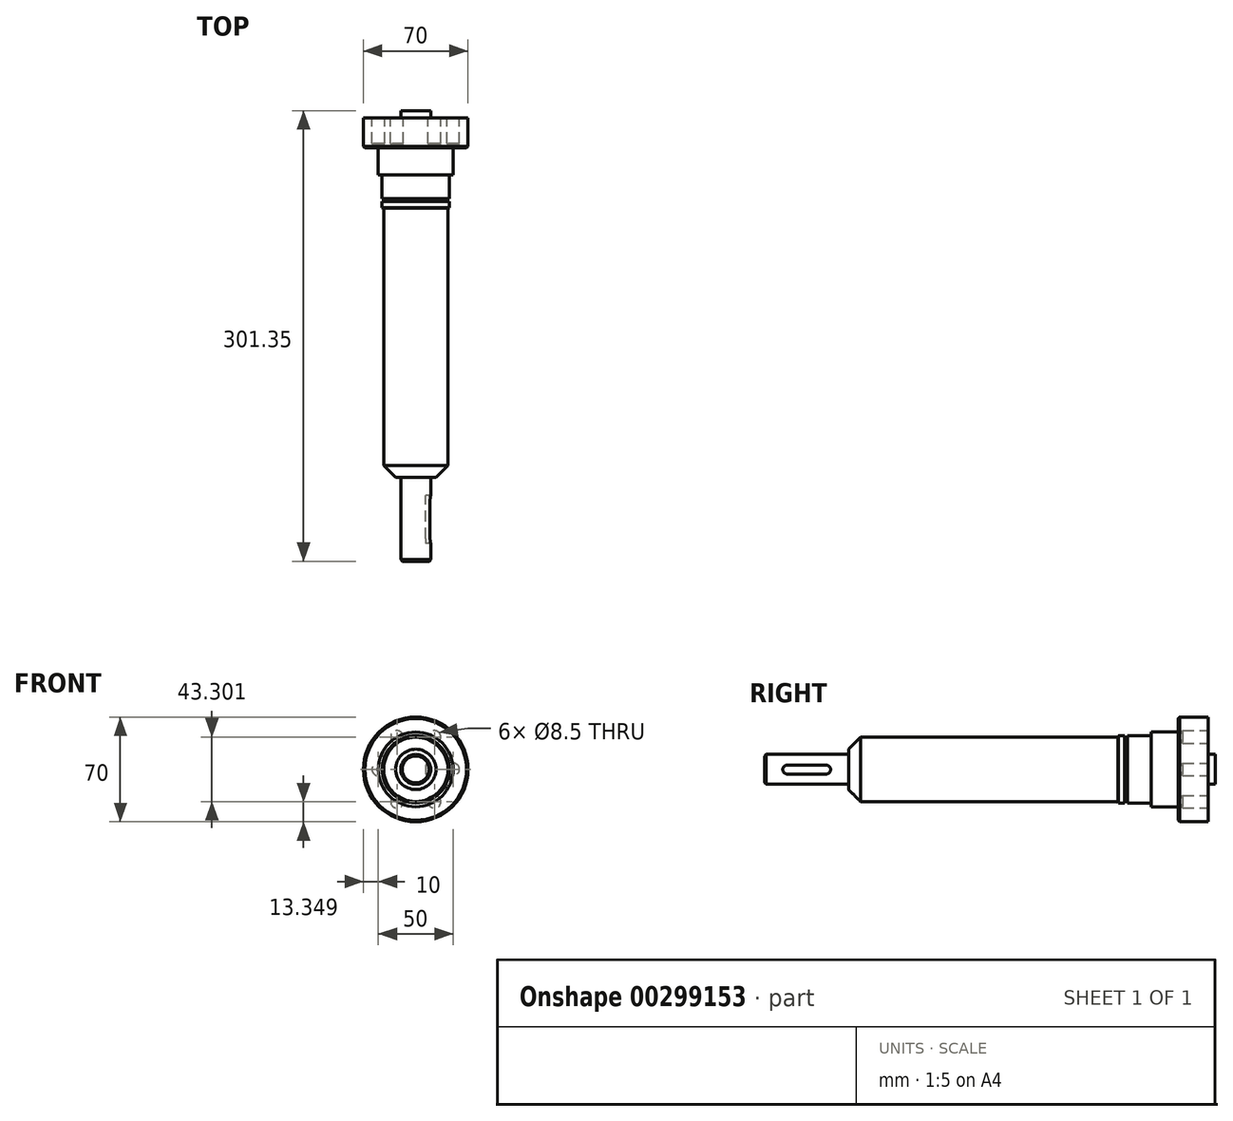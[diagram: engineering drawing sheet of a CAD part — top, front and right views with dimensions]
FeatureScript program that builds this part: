
annotation { "Feature Type Name" : "Feature", "Feature Type Description" : "" }
export const myFeature = defineFeature(function(context is Context, id is Id, definition is map)
    precondition{}
    {
        {
            var Q0;
            Q0=qCreatedBy(makeId("Front.planeOp"),FACE);
            var sketch = newSketch(context, id + "F0", { "sketchPlane" : qUnion([Q0])});
            skCircle(sketch, "E0", {"center": v(0, 0) * mm, "radius": 10 * mm});
            skSolve(sketch);
        }
        {
            var Q0;
            Q0 = qSketchRegion(id + "F0", true);
            extrude(context, id + "F1", {"entities" : qUnion([Q0]), "depth" : 56 * mm});
        }
        {
            var Q0;
            Q0=qCreatedBy(makeId("Front.planeOp"),FACE);
            var sketch = newSketch(context, id + "F2", { "sketchPlane" : qUnion([Q0])});
            skCircle(sketch, "E1", {"center": v(0, 0) * mm, "radius": 21.5 * mm});
            skSolve(sketch);
        }
        {
            var Q0;
            Q0 = qSketchRegion(id + "F2", true);
            extrude(context, id + "F3", {"entities" : qUnion([Q0]), "operationType" : NewBodyOperationType.ADD, "oppositeDirection" : true, "depth" : 180 * mm});
        }
        {
            var Q0;
            Q0=makeQuery(id+"F3.opExtrude","CAP_EDGE",EDGE,{"disambiguationData":[OSD([sQuery(id+"F2.wireOp",EDGE,"E1")])],"isStart":true});
            chamfer(context, id + "F4", {"entities" : qUnion([Q0]), "width" : 8 * mm, "tangentPropagation" : true});
        }
        {
            var Q0;
            Q0=makeQuery(id+"F3.opExtrude","CAP_FACE",FACE,{"disambiguationData":[OSD([sQuery(id+"F2.wireOp",EDGE,"E1")])],"isStart":false});
            cPlane(context, id + "F5", {"entities" : qUnion([Q0]), "cplaneType" : CPlaneType.OFFSET, "offset" : 0 * mm, "width" : 150 * mm, "height" : 150 * mm});
        }
        {
            var Q0;
            Q0=qCreatedBy(id+"F5.planeOp",FACE);
            var sketch = newSketch(context, id + "F6", { "sketchPlane" : qUnion([Q0])});
            skCircle(sketch, "E2", {"center": v(0, 0) * mm, "radius": 22.5 * mm});
            skSolve(sketch);
        }
        {
            var Q0;
            Q0 = qSketchRegion(id + "F6", true);
            extrude(context, id + "F7", {"entities" : qUnion([Q0]), "operationType" : NewBodyOperationType.ADD, "depth" : 40.35 * mm});
        }
        {
            var Q0;
            Q0=makeQuery(id+"F7.opExtrude","CAP_FACE",FACE,{"disambiguationData":[OSD([sQuery(id+"F6.wireOp",EDGE,"E2")])],"isStart":false});
            var sketch = newSketch(context, id + "F8", { "sketchPlane" : qUnion([Q0])});
            skCircle(sketch, "E3", {"center": v(0, 0) * mm, "radius": 35 * mm});
            skSolve(sketch);
        }
        {
            var Q0;
            Q0 = qSketchRegion(id + "F8", true);
            extrude(context, id + "F9", {"entities" : qUnion([Q0]), "operationType" : NewBodyOperationType.ADD, "depth" : 20 * mm});
        }
        {
            var Q0;
            Q0=qCreatedBy(id+"F5.planeOp",FACE);
            cPlane(context, id + "F10", {"entities" : qUnion([Q0]), "cplaneType" : CPlaneType.OFFSET, "offset" : 4.5 * mm, "width" : 150 * mm, "height" : 150 * mm});
        }
        {
            var Q0;
            Q0=qCreatedBy(id+"F10.planeOp",FACE);
            var sketch = newSketch(context, id + "F11", { "sketchPlane" : qUnion([Q0])});
            skCircle(sketch, "E4", {"center": v(0, 0) * mm, "radius": 21.25 * mm});
            skCircle(sketch, "E5", {"center": v(0, 0) * mm, "radius": 31 * mm});
            skSolve(sketch);
        }
        {
            var Q0;
            Q0 = qSketchRegion(id + "F11", true);
            extrude(context, id + "F12", {"entities" : qUnion([Q0]), "operationType" : NewBodyOperationType.REMOVE, "depth" : 1.85 * mm});
        }
        {
            var Q0;
            Q0=qCreatedBy(makeId("Right.planeOp"),FACE);
            cPlane(context, id + "F13", {"entities" : qUnion([Q0]), "cplaneType" : CPlaneType.OFFSET, "offset" : 6.5 * mm, "width" : 150 * mm, "height" : 150 * mm});
        }
        {
            var Q0;
            Q0=qCreatedBy(id+"F13.planeOp",FACE);
            var sketch = newSketch(context, id + "F14", { "sketchPlane" : qUnion([Q0])});
            skLineSegment(sketch, "E6", {"start": v(-41, 2.88) * mm, "end": v(-15, 2.88) * mm});
            skArc(sketch, "E7", {"start": v(-15, 2.88) * mm, "mid": v(-12, -0.12) * mm, "end": v(-15, -3.12) * mm});
            skLineSegment(sketch, "E8", {"start": v(-15, -3.12) * mm, "end": v(-41, -3.12) * mm});
            skArc(sketch, "E9", {"start": v(-41, 2.88) * mm, "mid": v(-44, -0.12) * mm, "end": v(-41, -3.12) * mm});
            skSolve(sketch);
        }
        {
            var Q0;
            Q0 = qSketchRegion(id + "F14", true);
            extrude(context, id + "F15", {"entities" : qUnion([Q0]), "operationType" : NewBodyOperationType.REMOVE, "depth" : 25 * mm});
        }
        {
            var Q0;
            Q0=makeQuery(id+"F1.opExtrude","CAP_EDGE",EDGE,{"disambiguationData":[OSD([sQuery(id+"F0.wireOp",EDGE,"E0")])],"isStart":false});
            chamfer(context, id + "F16", {"entities" : qUnion([Q0]), "width" : 1 * mm, "tangentPropagation" : true});
        }
        {
            var Q0;
            Q0=makeQuery(id+"F9.opExtrude","CAP_FACE",FACE,{"disambiguationData":[OSD([sQuery(id+"F8.wireOp",EDGE,"E3")])],"isStart":false});
            var sketch = newSketch(context, id + "F17", { "sketchPlane" : qUnion([Q0])});
            skCircle(sketch, "E10", {"center": v(0, 0) * mm, "radius": 10 * mm});
            skSolve(sketch);
        }
        {
            var Q0;
            Q0=makeQuery(id+"F7.opExtrude","CAP_EDGE",EDGE,{"disambiguationData":[OSD([sQuery(id+"F6.wireOp",EDGE,"E2")])],"isStart":true});
            chamfer(context, id + "F18", {"entities" : qUnion([Q0]), "width" : 0.5 * mm, "tangentPropagation" : true});
        }
        {
            var Q0;
            Q0 = qSketchRegion(id + "F17", true);
            extrude(context, id + "F19", {"entities" : qUnion([Q0]), "operationType" : NewBodyOperationType.ADD, "depth" : 5 * mm});
        }
        {
            var Q0;
            Q0=makeQuery(id+"F9.opExtrude","CAP_FACE",FACE,{"disambiguationData":[OSD([sQuery(id+"F8.wireOp",EDGE,"E3")])],"isStart":false});
            cPlane(context, id + "F20", {"entities" : qUnion([Q0]), "cplaneType" : CPlaneType.OFFSET, "offset" : 0 * mm, "width" : 150 * mm, "height" : 150 * mm});
        }
        {
            var Q0;
            Q0=qCreatedBy(id+"F20.planeOp",FACE);
            var sketch = newSketch(context, id + "F21", { "sketchPlane" : qUnion([Q0])});
            skCircle(sketch, "E11", {"center": v(25, 0) * mm, "radius": 4.25 * mm});
            skCircle(sketch, "E12.1.0", {"center": v(12.5, 21.65) * mm, "radius": 4.25 * mm});
            skCircle(sketch, "E12.2.0", {"center": v(-12.5, 21.65) * mm, "radius": 4.25 * mm});
            skCircle(sketch, "E12.3.0", {"center": v(-25, 0) * mm, "radius": 4.25 * mm});
            skCircle(sketch, "E12.4.0", {"center": v(-12.5, -21.65) * mm, "radius": 4.25 * mm});
            skCircle(sketch, "E12.5.0", {"center": v(12.5, -21.65) * mm, "radius": 4.25 * mm});
            skPoint(sketch, "E12.center", {"position": v(0, 0) * mm});
            skSolve(sketch);
        }
        {
            var Q0;
            Q0=sQuery(id+"F21.wireOp",VERTEX,"E12.2.0.center");
            var Q1;
            Q1=sQuery(id+"F21.wireOp",VERTEX,"E12.1.0.center");
            var Q2;
            Q2=sQuery(id+"F21.wireOp",VERTEX,"E11.center");
            var Q3;
            Q3=sQuery(id+"F21.wireOp",VERTEX,"E12.5.0.center");
            var Q4;
            Q4=sQuery(id+"F21.wireOp",VERTEX,"E12.4.0.center");
            var Q5;
            Q5=sQuery(id+"F21.wireOp",VERTEX,"E12.3.0.center");
            var Q6;
            Q6=makeQuery(id+"F1.opExtrude","SWEPT_BODY",BODY,{"disambiguationData":[OSD([sQuery(id+"F0.wireOp",EDGE,"E0")])]});
            hole(context, id + "F22", {"style" : HoleStyle.SIMPLE, "endStyle" : HoleEndStyle.BLIND, "holeDiameter" : 8.5 * mm, "holeDepth" : 17 * mm, "isTappedThrough" : true, "tappedDepth" : 12 * mm, "tapClearance" : 3, "locations" : qUnion([Q0, Q1, Q2, Q3, Q4, Q5]), "scope" : qUnion([Q6])});
        }
        {
            var Q0;
            Q0=makeQuery(id+"F9.opExtrude","CAP_EDGE",EDGE,{"disambiguationData":[OSD([sQuery(id+"F8.wireOp",EDGE,"E3")])],"isStart":true});
            chamfer(context, id + "F23", {"entities" : qUnion([Q0]), "width" : 1 * mm, "tangentPropagation" : true});
        }
        {
            var Q0;
            Q0=makeQuery(id+"F12.boolean.opBoolean","COPY",FACE,{"derivedFrom":makeQuery(id+"F12.opExtrude","CAP_FACE",FACE,{"disambiguationData":[OSD([sQuery(id+"F11.wireOp",EDGE,"E4"),sQuery(id+"F11.wireOp",EDGE,"E5")])],"isStart":false})});
            cPlane(context, id + "F24", {"entities" : qUnion([Q0]), "cplaneType" : CPlaneType.OFFSET, "offset" : 16 * mm, "oppositeDirection" : true, "width" : 150 * mm, "height" : 150 * mm});
        }
        {
            var Q0;
            Q0=qCreatedBy(id+"F24.planeOp",FACE);
            var sketch = newSketch(context, id + "F25", { "sketchPlane" : qUnion([Q0])});
            skCircle(sketch, "E13", {"center": v(0, 0) * mm, "radius": 25 * mm});
            skSolve(sketch);
        }
        {
            var Q0;
            Q0 = qSketchRegion(id + "F25", true);
            extrude(context, id + "F26", {"entities" : qUnion([Q0]), "operationType" : NewBodyOperationType.ADD, "oppositeDirection" : true, "depth" : 18 * mm});
        }
    });
